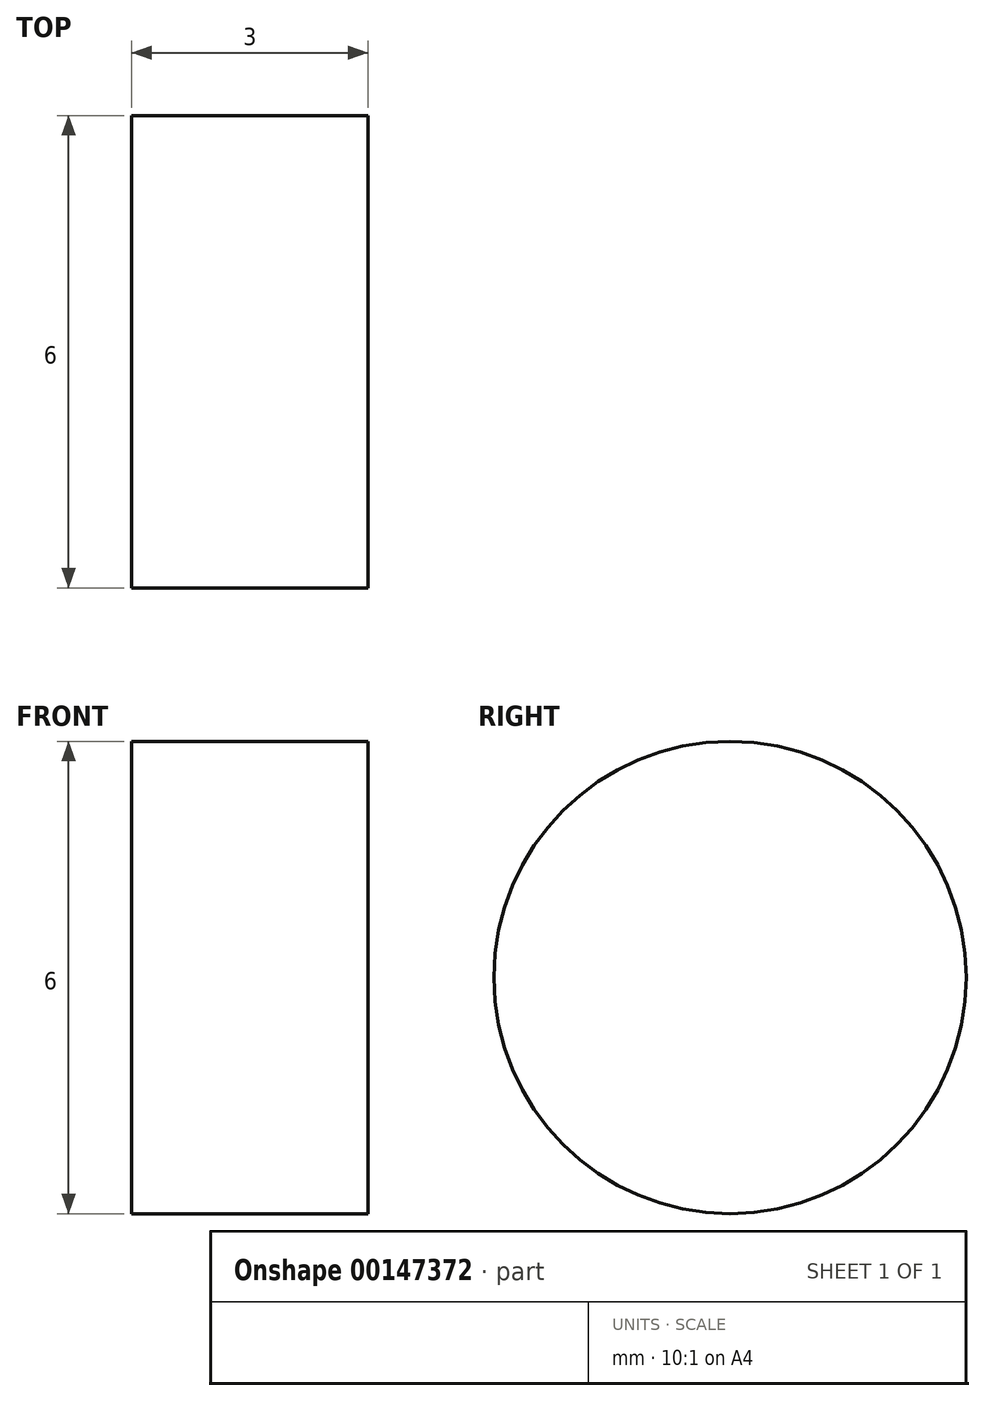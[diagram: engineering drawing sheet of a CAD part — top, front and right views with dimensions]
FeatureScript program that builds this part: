
annotation { "Feature Type Name" : "Feature", "Feature Type Description" : "" }
export const myFeature = defineFeature(function(context is Context, id is Id, definition is map)
    precondition{}
    {
        {
            var Q0;
            Q0=qCreatedBy(makeId("Right.planeOp"),FACE);
            var sketch = newSketch(context, id + "F0", { "sketchPlane" : qUnion([Q0])});
            skCircle(sketch, "E0", {"center": v(0, 0) * mm, "radius": 3 * mm});
            skSolve(sketch);
        }
        {
            var Q0;
            Q0 = qSketchRegion(id + "F0", true);
            extrude(context, id + "F1", {"entities" : qUnion([Q0]), "depth" : 3 * mm});
        }
    });
